# Revit family: Legrand Flush-mounting cabinets Nedbox
name_source: partatom
category: Installations électriques
units: mm (PartAtom-declared; Revit-internal decimal feet)

## family parameters
Basée sur le plan de construction = Non
Conserver l'orientation des annotations = Non
Cote de connecteur circulaire = Utiliser le diamètre
Couper avec des vides une fois chargée = Non
Numéro OmniClass = 23.80.00.00
Partagée = Non
Point de calcul de pièce = Non
Titre OmniClass = Electric Power and Lighting
Toujours verticalement = Oui
Type d'élément = Normal

## types (40) — shared parameters
Assembly Plastic door 1R 8M = Non
Assembly Plastic door transparent 1R 8M = Non
Fabricant = Legrand
Maximum permissible current = 63 A
Modèle = Nedbox
Number of modules per row = 12+2
Recessed depth = 90 mm  [stored 0.295276 ft]
Recessed width = 330 mm
URL = www.legrand.com
width = 350 mm  [stored 1.14829 ft]
zero-valued in all types: Elévation par défaut

## per-type parameters (varying)
- Flush-mounting cabinet Nedbox 12 modules Plastic door 001411: Assembly Plastic door 1R=Oui; Assembly Plastic door 2R=Non; Assembly Plastic door 3R=Non; Assembly Plastic door 4R=Non; Assembly Plastic door transparent 1R=Non; Assembly Plastic door transparent 2R=Non; Assembly Plastic door transparent 3R=Non; Assembly Plastic door transparent 4R=Non; Assembly glass metal door 1R=Non; Assembly glass metal door 2R=Non; Assembly glass metal door 3R=Non; Assembly glass metal door 4R=Non; Assembly metal door 1R=Non; Assembly metal door 2R=Non; Assembly metal door 3R=Non; Assembly metal door 4R=Non; Cabinet 001411=Oui; Cabinet 001412=Non; Cabinet 001413=Non; Cabinet 001414=Non; Cabinet 001421=Non; Cabinet 001422=Non; Cabinet 001423=Non; Cabinet 001424=Non; Cabinet 001431=Non; Cabinet 001432=Non; Cabinet 001433=Non; Cabinet 001434=Non; Cabinet 001436=Non; Cabinet 001437=Non; Cabinet 001438=Non; Cabinet 001439=Non; Cabinet 001441=Non; Cabinet 001442=Non; Cabinet 001443=Non; Cabinet 001444=Non; Cabinet 001451=Non; Cabinet 001452=Non; Cabinet 001453=Non; Cabinet 001454=Non; Cabinet 201411=Non; Cabinet 201412=Non; Cabinet 201413=Non; Cabinet 201414=Non; Cabinet 201421=Non; Cabinet 201422=Non; Cabinet 201423=Non; Cabinet 201424=Non; Cabinet 201431=Non; Cabinet 201432=Non; Cabinet 201433=Non; Cabinet 201434=Non; Cabinet HL12F=Non; Cabinet HL24F=Non; Cabinet HL36F=Non; Cabinet HL48F=Non; Number of rows=1; Plastic door=Oui; Recessed height=305 mm  [stored 1.00066 ft]; Terminal block E=13 connections Icc 10kA; glass metal door=Non; height=335 mm  [stored 1.09908 ft]; metal door=Non; transparent door=Non
- Flush-mounting cabinet Nedbox 24 modules Plastic door 001412: Assembly Plastic door 1R=Non; Assembly Plastic door 2R=Oui; Assembly Plastic door 3R=Non; Assembly Plastic door 4R=Non; Assembly Plastic door transparent 1R=Non; Assembly Plastic door transparent 2R=Non; Assembly Plastic door transparent 3R=Non; Assembly Plastic door transparent 4R=Non; Assembly glass metal door 1R=Non; Assembly glass metal door 2R=Non; Assembly glass metal door 3R=Non; Assembly glass metal door 4R=Non; Assembly metal door 1R=Non; Assembly metal door 2R=Non; Assembly metal door 3R=Non; Assembly metal door 4R=Non; Cabinet 001411=Non; Cabinet 001412=Oui; Cabinet 001413=Non; Cabinet 001414=Non; Cabinet 001421=Non; Cabinet 001422=Non; Cabinet 001423=Non; Cabinet 001424=Non; Cabinet 001431=Non; Cabinet 001432=Non; Cabinet 001433=Non; Cabinet 001434=Non; Cabinet 001436=Non; Cabinet 001437=Non; Cabinet 001438=Non; Cabinet 001439=Non; Cabinet 001441=Non; Cabinet 001442=Non; Cabinet 001443=Non; Cabinet 001444=Non; Cabinet 001451=Non; Cabinet 001452=Non; Cabinet 001453=Non; Cabinet 001454=Non; Cabinet 201411=Non; Cabinet 201412=Non; Cabinet 201413=Non; Cabinet 201414=Non; Cabinet 201421=Non; Cabinet 201422=Non; Cabinet 201423=Non; Cabinet 201424=Non; Cabinet 201431=Non; Cabinet 201432=Non; Cabinet 201433=Non; Cabinet 201434=Non; Cabinet HL12F=Non; Cabinet HL24F=Non; Cabinet HL36F=Non; Cabinet HL48F=Non; General Conditions of Use=https://export.legrand.com; Number of rows=2; Plastic door=Oui; Recessed height=430 mm; Terminal block E=17 connections Icc 10kA; glass metal door=Non; height=460 mm  [stored 1.50919 ft]; metal door=Non; transparent door=Non
- Flush-mounting cabinet Nedbox 36 modules Plastic door 001413: Assembly Plastic door 1R=Non; Assembly Plastic door 2R=Non; Assembly Plastic door 3R=Oui; Assembly Plastic door 4R=Non; Assembly Plastic door transparent 1R=Non; Assembly Plastic door transparent 2R=Non; Assembly Plastic door transparent 3R=Non; Assembly Plastic door transparent 4R=Non; Assembly glass metal door 1R=Non; Assembly glass metal door 2R=Non; Assembly glass metal door 3R=Non; Assembly glass metal door 4R=Non; Assembly metal door 1R=Non; Assembly metal door 2R=Non; Assembly metal door 3R=Non; Assembly metal door 4R=Non; Cabinet 001411=Non; Cabinet 001412=Non; Cabinet 001413=Oui; Cabinet 001414=Non; Cabinet 001421=Non; Cabinet 001422=Non; Cabinet 001423=Non; Cabinet 001424=Non; Cabinet 001431=Non; Cabinet 001432=Non; Cabinet 001433=Non; Cabinet 001434=Non; Cabinet 001436=Non; Cabinet 001437=Non; Cabinet 001438=Non; Cabinet 001439=Non; Cabinet 001441=Non; Cabinet 001442=Non; Cabinet 001443=Non; Cabinet 001444=Non; Cabinet 001451=Non; Cabinet 001452=Non; Cabinet 001453=Non; Cabinet 001454=Non; Cabinet 201411=Non; Cabinet 201412=Non; Cabinet 201413=Non; Cabinet 201414=Non; Cabinet 201421=Non; Cabinet 201422=Non; Cabinet 201423=Non; Cabinet 201424=Non; Cabinet 201431=Non; Cabinet 201432=Non; Cabinet 201433=Non; Cabinet 201434=Non; Cabinet HL12F=Non; Cabinet HL24F=Non; Cabinet HL36F=Non; Cabinet HL48F=Non; General Conditions of Use=https://export.legrand.com; Number of rows=3; Plastic door=Oui; Recessed height=555 mm  [stored 1.82087 ft]; Terminal block E=22 connections Icc 10kA; glass metal door=Non; height=585 mm  [stored 1.91929 ft]; metal door=Non; transparent door=Non
- Flush-mounting cabinet Nedbox 48 modules Plastic door 001414: Assembly Plastic door 1R=Non; Assembly Plastic door 2R=Non; Assembly Plastic door 3R=Non; Assembly Plastic door 4R=Oui; Assembly Plastic door transparent 1R=Non; Assembly Plastic door transparent 2R=Non; Assembly Plastic door transparent 3R=Non; Assembly Plastic door transparent 4R=Non; Assembly glass metal door 1R=Non; Assembly glass metal door 2R=Non; Assembly glass metal door 3R=Non; Assembly glass metal door 4R=Non; Assembly metal door 1R=Non; Assembly metal door 2R=Non; Assembly metal door 3R=Non; Assembly metal door 4R=Non; Cabinet 001411=Non; Cabinet 001412=Non; Cabinet 001413=Non; Cabinet 001414=Oui; Cabinet 001421=Non; Cabinet 001422=Non; Cabinet 001423=Non; Cabinet 001424=Non; Cabinet 001431=Non; Cabinet 001432=Non; Cabinet 001433=Non; Cabinet 001434=Non; Cabinet 001436=Non; Cabinet 001437=Non; Cabinet 001438=Non; Cabinet 001439=Non; Cabinet 001441=Non; Cabinet 001442=Non; Cabinet 001443=Non; Cabinet 001444=Non; Cabinet 001451=Non; Cabinet 001452=Non; Cabinet 001453=Non; Cabinet 001454=Non; Cabinet 201411=Non; Cabinet 201412=Non; Cabinet 201413=Non; Cabinet 201414=Non; Cabinet 201421=Non; Cabinet 201422=Non; Cabinet 201423=Non; Cabinet 201424=Non; Cabinet 201431=Non; Cabinet 201432=Non; Cabinet 201433=Non; Cabinet 201434=Non; Cabinet HL12F=Non; Cabinet HL24F=Non; Cabinet HL36F=Non; Cabinet HL48F=Non; General Conditions of Use=https://export.legrand.com; Number of rows=4; Plastic door=Oui; Recessed height=680 mm  [stored 2.23097 ft]; Terminal block E=27 connections Icc 10kA; glass metal door=Non; height=710 mm  [stored 2.3294 ft]; metal door=Non; transparent door=Non
- Flush-mounting cabinet Nedbox 12 modules transparent door 001421: Assembly Plastic door 1R=Non; Assembly Plastic door 2R=Non; Assembly Plastic door 3R=Non; Assembly Plastic door 4R=Non; Assembly Plastic door transparent 1R=Oui; Assembly Plastic door transparent 2R=Non; Assembly Plastic door transparent 3R=Non; Assembly Plastic door transparent 4R=Non; Assembly glass metal door 1R=Non; Assembly glass metal door 2R=Non; Assembly glass metal door 3R=Non; Assembly glass metal door 4R=Non; Assembly metal door 1R=Non; Assembly metal door 2R=Non; Assembly metal door 3R=Non; Assembly metal door 4R=Non; Cabinet 001411=Non; Cabinet 001412=Non; Cabinet 001413=Non; Cabinet 001414=Non; Cabinet 001421=Oui; Cabinet 001422=Non; Cabinet 001423=Non; Cabinet 001424=Non; Cabinet 001431=Non; Cabinet 001432=Non; Cabinet 001433=Non; Cabinet 001434=Non; Cabinet 001436=Non; Cabinet 001437=Non; Cabinet 001438=Non; Cabinet 001439=Non; Cabinet 001441=Non; Cabinet 001442=Non; Cabinet 001443=Non; Cabinet 001444=Non; Cabinet 001451=Non; Cabinet 001452=Non; Cabinet 001453=Non; Cabinet 001454=Non; Cabinet 201411=Non; Cabinet 201412=Non; Cabinet 201413=Non; Cabinet 201414=Non; Cabinet 201421=Non; Cabinet 201422=Non; Cabinet 201423=Non; Cabinet 201424=Non; Cabinet 201431=Non; Cabinet 201432=Non; Cabinet 201433=Non; Cabinet 201434=Non; Cabinet HL12F=Non; Cabinet HL24F=Non; Cabinet HL36F=Non; Cabinet HL48F=Non; Number of rows=1; Plastic door=Non; Recessed height=305 mm  [stored 1.00066 ft]; Terminal block E=8 connections Icc 10kA; glass metal door=Non; height=335 mm  [stored 1.09908 ft]; metal door=Non; transparent door=Oui
- Flush-mounting cabinet Nedbox 24 modules transparent door 001422: Assembly Plastic door 1R=Non; Assembly Plastic door 2R=Non; Assembly Plastic door 3R=Non; Assembly Plastic door 4R=Non; Assembly Plastic door transparent 1R=Non; Assembly Plastic door transparent 2R=Oui; Assembly Plastic door transparent 3R=Non; Assembly Plastic door transparent 4R=Non; Assembly glass metal door 1R=Non; Assembly glass metal door 2R=Non; Assembly glass metal door 3R=Non; Assembly glass metal door 4R=Non; Assembly metal door 1R=Non; Assembly metal door 2R=Non; Assembly metal door 3R=Non; Assembly metal door 4R=Non; Cabinet 001411=Non; Cabinet 001412=Non; Cabinet 001413=Non; Cabinet 001414=Non; Cabinet 001421=Non; Cabinet 001422=Oui; Cabinet 001423=Non; Cabinet 001424=Non; Cabinet 001431=Non; Cabinet 001432=Non; Cabinet 001433=Non; Cabinet 001434=Non; Cabinet 001436=Non; Cabinet 001437=Non; Cabinet 001438=Non; Cabinet 001439=Non; Cabinet 001441=Non; Cabinet 001442=Non; Cabinet 001443=Non; Cabinet 001444=Non; Cabinet 001451=Non; Cabinet 001452=Non; Cabinet 001453=Non; Cabinet 001454=Non; Cabinet 201411=Non; Cabinet 201412=Non; Cabinet 201413=Non; Cabinet 201414=Non; Cabinet 201421=Non; Cabinet 201422=Non; Cabinet 201423=Non; Cabinet 201424=Non; Cabinet 201431=Non; Cabinet 201432=Non; Cabinet 201433=Non; Cabinet 201434=Non; Cabinet HL12F=Non; Cabinet HL24F=Non; Cabinet HL36F=Non; Cabinet HL48F=Non; General Conditions of Use=https://export.legrand.com; Number of rows=2; Plastic door=Non; Recessed height=430 mm; Terminal block E=17 connections Icc 10kA; glass metal door=Non; height=460 mm  [stored 1.50919 ft]; metal door=Non; transparent door=Oui
- Flush-mounting cabinet Nedbox 36 modules transparent door 001423: Assembly Plastic door 1R=Non; Assembly Plastic door 2R=Non; Assembly Plastic door 3R=Non; Assembly Plastic door 4R=Non; Assembly Plastic door transparent 1R=Non; Assembly Plastic door transparent 2R=Non; Assembly Plastic door transparent 3R=Oui; Assembly Plastic door transparent 4R=Non; Assembly glass metal door 1R=Non; Assembly glass metal door 2R=Non; Assembly glass metal door 3R=Non; Assembly glass metal door 4R=Non; Assembly metal door 1R=Non; Assembly metal door 2R=Non; Assembly metal door 3R=Non; Assembly metal door 4R=Non; Cabinet 001411=Non; Cabinet 001412=Non; Cabinet 001413=Non; Cabinet 001414=Non; Cabinet 001421=Non; Cabinet 001422=Non; Cabinet 001423=Oui; Cabinet 001424=Non; Cabinet 001431=Non; Cabinet 001432=Non; Cabinet 001433=Non; Cabinet 001434=Non; Cabinet 001436=Non; Cabinet 001437=Non; Cabinet 001438=Non; Cabinet 001439=Non; Cabinet 001441=Non; Cabinet 001442=Non; Cabinet 001443=Non; Cabinet 001444=Non; Cabinet 001451=Non; Cabinet 001452=Non; Cabinet 001453=Non; Cabinet 001454=Non; Cabinet 201411=Non; Cabinet 201412=Non; Cabinet 201413=Non; Cabinet 201414=Non; Cabinet 201421=Non; Cabinet 201422=Non; Cabinet 201423=Non; Cabinet 201424=Non; Cabinet 201431=Non; Cabinet 201432=Non; Cabinet 201433=Non; Cabinet 201434=Non; Cabinet HL12F=Non; Cabinet HL24F=Non; Cabinet HL36F=Non; Cabinet HL48F=Non; General Conditions of Use=https://export.legrand.com; Number of rows=3; Plastic door=Non; Recessed height=555 mm  [stored 1.82087 ft]; Terminal block E=22 connections Icc 10kA; glass metal door=Non; height=585 mm  [stored 1.91929 ft]; metal door=Non; transparent door=Oui
- Flush-mounting cabinet Nedbox 48 modules transparent door 001424: Assembly Plastic door 1R=Non; Assembly Plastic door 2R=Non; Assembly Plastic door 3R=Non; Assembly Plastic door 4R=Non; Assembly Plastic door transparent 1R=Non; Assembly Plastic door transparent 2R=Non; Assembly Plastic door transparent 3R=Non; Assembly Plastic door transparent 4R=Oui; Assembly glass metal door 1R=Non; Assembly glass metal door 2R=Non; Assembly glass metal door 3R=Non; Assembly glass metal door 4R=Non; Assembly metal door 1R=Non; Assembly metal door 2R=Non; Assembly metal door 3R=Non; Assembly metal door 4R=Non; Cabinet 001411=Non; Cabinet 001412=Non; Cabinet 001413=Non; Cabinet 001414=Non; Cabinet 001421=Non; Cabinet 001422=Non; Cabinet 001423=Non; Cabinet 001424=Oui; Cabinet 001431=Non; Cabinet 001432=Non; Cabinet 001433=Non; Cabinet 001434=Non; Cabinet 001436=Non; Cabinet 001437=Non; Cabinet 001438=Non; Cabinet 001439=Non; Cabinet 001441=Non; Cabinet 001442=Non; Cabinet 001443=Non; Cabinet 001444=Non; Cabinet 001451=Non; Cabinet 001452=Non; Cabinet 001453=Non; Cabinet 001454=Non; Cabinet 201411=Non; Cabinet 201412=Non; Cabinet 201413=Non; Cabinet 201414=Non; Cabinet 201421=Non; Cabinet 201422=Non; Cabinet 201423=Non; Cabinet 201424=Non; Cabinet 201431=Non; Cabinet 201432=Non; Cabinet 201433=Non; Cabinet 201434=Non; Cabinet HL12F=Non; Cabinet HL24F=Non; Cabinet HL36F=Non; Cabinet HL48F=Non; General Conditions of Use=https://export.legrand.com; Number of rows=4; Plastic door=Non; Recessed height=680 mm  [stored 2.23097 ft]; Terminal block E=27 connections Icc 10kA; glass metal door=Non; height=710 mm  [stored 2.3294 ft]; metal door=Non; transparent door=Oui
- Flush-mounting cabinet Nedbox 12 modules metal door 001431: Assembly Plastic door 1R=Non; Assembly Plastic door 2R=Non; Assembly Plastic door 3R=Non; Assembly Plastic door 4R=Non; Assembly Plastic door transparent 1R=Non; Assembly Plastic door transparent 2R=Non; Assembly Plastic door transparent 3R=Non; Assembly Plastic door transparent 4R=Non; Assembly glass metal door 1R=Non; Assembly glass metal door 2R=Non; Assembly glass metal door 3R=Non; Assembly glass metal door 4R=Non; Assembly metal door 1R=Oui; Assembly metal door 2R=Non; Assembly metal door 3R=Non; Assembly metal door 4R=Non; Cabinet 001411=Non; Cabinet 001412=Non; Cabinet 001413=Non; Cabinet 001414=Non; Cabinet 001421=Non; Cabinet 001422=Non; Cabinet 001423=Non; Cabinet 001424=Non; Cabinet 001431=Oui; Cabinet 001432=Non; Cabinet 001433=Non; Cabinet 001434=Non; Cabinet 001436=Non; Cabinet 001437=Non; Cabinet 001438=Non; Cabinet 001439=Non; Cabinet 001441=Non; Cabinet 001442=Non; Cabinet 001443=Non; Cabinet 001444=Non; Cabinet 001451=Non; Cabinet 001452=Non; Cabinet 001453=Non; Cabinet 001454=Non; Cabinet 201411=Non; Cabinet 201412=Non; Cabinet 201413=Non; Cabinet 201414=Non; Cabinet 201421=Non; Cabinet 201422=Non; Cabinet 201423=Non; Cabinet 201424=Non; Cabinet 201431=Non; Cabinet 201432=Non; Cabinet 201433=Non; Cabinet 201434=Non; Cabinet HL12F=Non; Cabinet HL24F=Non; Cabinet HL36F=Non; Cabinet HL48F=Non; Number of rows=1; Plastic door=Non; Recessed height=305 mm  [stored 1.00066 ft]; Terminal block E=13 connections Icc 10kA; glass metal door=Non; height=335 mm  [stored 1.09908 ft]; metal door=Oui; transparent door=Non
- Flush-mounting cabinet Nedbox 24 modules metal door 001432: Assembly Plastic door 1R=Non; Assembly Plastic door 2R=Non; Assembly Plastic door 3R=Non; Assembly Plastic door 4R=Non; Assembly Plastic door transparent 1R=Non; Assembly Plastic door transparent 2R=Non; Assembly Plastic door transparent 3R=Non; Assembly Plastic door transparent 4R=Non; Assembly glass metal door 1R=Non; Assembly glass metal door 2R=Non; Assembly glass metal door 3R=Non; Assembly glass metal door 4R=Non; Assembly metal door 1R=Non; Assembly metal door 2R=Oui; Assembly metal door 3R=Non; Assembly metal door 4R=Non; Cabinet 001411=Non; Cabinet 001412=Non; Cabinet 001413=Non; Cabinet 001414=Non; Cabinet 001421=Non; Cabinet 001422=Non; Cabinet 001423=Non; Cabinet 001424=Non; Cabinet 001431=Non; Cabinet 001432=Oui; Cabinet 001433=Non; Cabinet 001434=Non; Cabinet 001436=Non; Cabinet 001437=Non; Cabinet 001438=Non; Cabinet 001439=Non; Cabinet 001441=Non; Cabinet 001442=Non; Cabinet 001443=Non; Cabinet 001444=Non; Cabinet 001451=Non; Cabinet 001452=Non; Cabinet 001453=Non; Cabinet 001454=Non; Cabinet 201411=Non; Cabinet 201412=Non; Cabinet 201413=Non; Cabinet 201414=Non; Cabinet 201421=Non; Cabinet 201422=Non; Cabinet 201423=Non; Cabinet 201424=Non; Cabinet 201431=Non; Cabinet 201432=Non; Cabinet 201433=Non; Cabinet 201434=Non; Cabinet HL12F=Non; Cabinet HL24F=Non; Cabinet HL36F=Non; Cabinet HL48F=Non; General Conditions of Use=https://export.legrand.com; Number of rows=2; Plastic door=Non; Recessed height=430 mm; Terminal block E=17 connections Icc 10kA; glass metal door=Non; height=460 mm  [stored 1.50919 ft]; metal door=Oui; transparent door=Non
- Flush-mounting cabinet Nedbox 36 modules metal door 001433: Assembly Plastic door 1R=Non; Assembly Plastic door 2R=Non; Assembly Plastic door 3R=Non; Assembly Plastic door 4R=Non; Assembly Plastic door transparent 1R=Non; Assembly Plastic door transparent 2R=Non; Assembly Plastic door transparent 3R=Non; Assembly Plastic door transparent 4R=Non; Assembly glass metal door 1R=Non; Assembly glass metal door 2R=Non; Assembly glass metal door 3R=Non; Assembly glass metal door 4R=Non; Assembly metal door 1R=Non; Assembly metal door 2R=Non; Assembly metal door 3R=Oui; Assembly metal door 4R=Non; Cabinet 001411=Non; Cabinet 001412=Non; Cabinet 001413=Non; Cabinet 001414=Non; Cabinet 001421=Non; Cabinet 001422=Non; Cabinet 001423=Non; Cabinet 001424=Non; Cabinet 001431=Non; Cabinet 001432=Non; Cabinet 001433=Oui; Cabinet 001434=Non; Cabinet 001436=Non; Cabinet 001437=Non; Cabinet 001438=Non; Cabinet 001439=Non; Cabinet 001441=Non; Cabinet 001442=Non; Cabinet 001443=Non; Cabinet 001444=Non; Cabinet 001451=Non; Cabinet 001452=Non; Cabinet 001453=Non; Cabinet 001454=Non; Cabinet 201411=Non; Cabinet 201412=Non; Cabinet 201413=Non; Cabinet 201414=Non; Cabinet 201421=Non; Cabinet 201422=Non; Cabinet 201423=Non; Cabinet 201424=Non; Cabinet 201431=Non; Cabinet 201432=Non; Cabinet 201433=Non; Cabinet 201434=Non; Cabinet HL12F=Non; Cabinet HL24F=Non; Cabinet HL36F=Non; Cabinet HL48F=Non; General Conditions of Use=https://export.legrand.com; Number of rows=3; Plastic door=Non; Recessed height=555 mm  [stored 1.82087 ft]; Terminal block E=22 connections Icc 10kA; glass metal door=Non; height=585 mm  [stored 1.91929 ft]; metal door=Oui; transparent door=Non
- Flush-mounting cabinet Nedbox 48 modules metal door 001434: Assembly Plastic door 1R=Non; Assembly Plastic door 2R=Non; Assembly Plastic door 3R=Non; Assembly Plastic door 4R=Non; Assembly Plastic door transparent 1R=Non; Assembly Plastic door transparent 2R=Non; Assembly Plastic door transparent 3R=Non; Assembly Plastic door transparent 4R=Non; Assembly glass metal door 1R=Non; Assembly glass metal door 2R=Non; Assembly glass metal door 3R=Non; Assembly glass metal door 4R=Non; Assembly metal door 1R=Non; Assembly metal door 2R=Non; Assembly metal door 3R=Non; Assembly metal door 4R=Oui; Cabinet 001411=Non; Cabinet 001412=Non; Cabinet 001413=Non; Cabinet 001414=Non; Cabinet 001421=Non; Cabinet 001422=Non; Cabinet 001423=Non; Cabinet 001424=Non; Cabinet 001431=Non; Cabinet 001432=Non; Cabinet 001433=Non; Cabinet 001434=Oui; Cabinet 001436=Non; Cabinet 001437=Non; Cabinet 001438=Non; Cabinet 001439=Non; Cabinet 001441=Non; Cabinet 001442=Non; Cabinet 001443=Non; Cabinet 001444=Non; Cabinet 001451=Non; Cabinet 001452=Non; Cabinet 001453=Non; Cabinet 001454=Non; Cabinet 201411=Non; Cabinet 201412=Non; Cabinet 201413=Non; Cabinet 201414=Non; Cabinet 201421=Non; Cabinet 201422=Non; Cabinet 201423=Non; Cabinet 201424=Non; Cabinet 201431=Non; Cabinet 201432=Non; Cabinet 201433=Non; Cabinet 201434=Non; Cabinet HL12F=Non; Cabinet HL24F=Non; Cabinet HL36F=Non; Cabinet HL48F=Non; General Conditions of Use=https://export.legrand.com; Number of rows=4; Plastic door=Non; Recessed height=680 mm  [stored 2.23097 ft]; Terminal block E=27 connections Icc 10kA; glass metal door=Non; height=710 mm  [stored 2.3294 ft]; metal door=Oui; transparent door=Non
- Flush-mounting cabinet Nedbox 12 modules metal door 001436: Assembly Plastic door 1R=Non; Assembly Plastic door 2R=Non; Assembly Plastic door 3R=Non; Assembly Plastic door 4R=Non; Assembly Plastic door transparent 1R=Non; Assembly Plastic door transparent 2R=Non; Assembly Plastic door transparent 3R=Non; Assembly Plastic door transparent 4R=Non; Assembly glass metal door 1R=Non; Assembly glass metal door 2R=Non; Assembly glass metal door 3R=Non; Assembly glass metal door 4R=Non; Assembly metal door 1R=Oui; Assembly metal door 2R=Non; Assembly metal door 3R=Non; Assembly metal door 4R=Non; Cabinet 001411=Non; Cabinet 001412=Non; Cabinet 001413=Non; Cabinet 001414=Non; Cabinet 001421=Non; Cabinet 001422=Non; Cabinet 001423=Non; Cabinet 001424=Non; Cabinet 001431=Non; Cabinet 001432=Non; Cabinet 001433=Non; Cabinet 001434=Non; Cabinet 001436=Oui; Cabinet 001437=Non; Cabinet 001438=Non; Cabinet 001439=Non; Cabinet 001441=Non; Cabinet 001442=Non; Cabinet 001443=Non; Cabinet 001444=Non; Cabinet 001451=Non; Cabinet 001452=Non; Cabinet 001453=Non; Cabinet 001454=Non; Cabinet 201411=Non; Cabinet 201412=Non; Cabinet 201413=Non; Cabinet 201414=Non; Cabinet 201421=Non; Cabinet 201422=Non; Cabinet 201423=Non; Cabinet 201424=Non; Cabinet 201431=Non; Cabinet 201432=Non; Cabinet 201433=Non; Cabinet 201434=Non; Cabinet HL12F=Non; Cabinet HL24F=Non; Cabinet HL36F=Non; Cabinet HL48F=Non; Number of rows=1; Plastic door=Non; Recessed height=305 mm  [stored 1.00066 ft]; Terminal block E=12 connections Icc 6kA; Terminal block N=12 connections Icc 6kA; glass metal door=Non; height=335 mm  [stored 1.09908 ft]; metal door=Oui; transparent door=Non
- Flush-mounting cabinet Nedbox 24 modules metal door 001437: Assembly Plastic door 1R=Non; Assembly Plastic door 2R=Non; Assembly Plastic door 3R=Non; Assembly Plastic door 4R=Non; Assembly Plastic door transparent 1R=Non; Assembly Plastic door transparent 2R=Non; Assembly Plastic door transparent 3R=Non; Assembly Plastic door transparent 4R=Non; Assembly glass metal door 1R=Non; Assembly glass metal door 2R=Non; Assembly glass metal door 3R=Non; Assembly glass metal door 4R=Non; Assembly metal door 1R=Non; Assembly metal door 2R=Oui; Assembly metal door 3R=Non; Assembly metal door 4R=Non; Cabinet 001411=Non; Cabinet 001412=Non; Cabinet 001413=Non; Cabinet 001414=Non; Cabinet 001421=Non; Cabinet 001422=Non; Cabinet 001423=Non; Cabinet 001424=Non; Cabinet 001431=Non; Cabinet 001432=Non; Cabinet 001433=Non; Cabinet 001434=Non; Cabinet 001436=Non; Cabinet 001437=Oui; Cabinet 001438=Non; Cabinet 001439=Non; Cabinet 001441=Non; Cabinet 001442=Non; Cabinet 001443=Non; Cabinet 001444=Non; Cabinet 001451=Non; Cabinet 001452=Non; Cabinet 001453=Non; Cabinet 001454=Non; Cabinet 201411=Non; Cabinet 201412=Non; Cabinet 201413=Non; Cabinet 201414=Non; Cabinet 201421=Non; Cabinet 201422=Non; Cabinet 201423=Non; Cabinet 201424=Non; Cabinet 201431=Non; Cabinet 201432=Non; Cabinet 201433=Non; Cabinet 201434=Non; Cabinet HL12F=Non; Cabinet HL24F=Non; Cabinet HL36F=Non; Cabinet HL48F=Non; General Conditions of Use=https://export.legrand.com; Number of rows=2; Plastic door=Non; Recessed height=430 mm; Terminal block E=16 connections Icc 6kA; Terminal block N=2X 8 connections Icc 6kA; glass metal door=Non; height=460 mm  [stored 1.50919 ft]; metal door=Oui; transparent door=Non
- Flush-mounting cabinet Nedbox 36 modules metal door 001438: Assembly Plastic door 1R=Non; Assembly Plastic door 2R=Non; Assembly Plastic door 3R=Non; Assembly Plastic door 4R=Non; Assembly Plastic door transparent 1R=Non; Assembly Plastic door transparent 2R=Non; Assembly Plastic door transparent 3R=Non; Assembly Plastic door transparent 4R=Non; Assembly glass metal door 1R=Non; Assembly glass metal door 2R=Non; Assembly glass metal door 3R=Non; Assembly glass metal door 4R=Non; Assembly metal door 1R=Non; Assembly metal door 2R=Non; Assembly metal door 3R=Oui; Assembly metal door 4R=Non; Cabinet 001411=Non; Cabinet 001412=Non; Cabinet 001413=Non; Cabinet 001414=Non; Cabinet 001421=Non; Cabinet 001422=Non; Cabinet 001423=Non; Cabinet 001424=Non; Cabinet 001431=Non; Cabinet 001432=Non; Cabinet 001433=Non; Cabinet 001434=Non; Cabinet 001436=Non; Cabinet 001437=Non; Cabinet 001438=Oui; Cabinet 001439=Non; Cabinet 001441=Non; Cabinet 001442=Non; Cabinet 001443=Non; Cabinet 001444=Non; Cabinet 001451=Non; Cabinet 001452=Non; Cabinet 001453=Non; Cabinet 001454=Non; Cabinet 201411=Non; Cabinet 201412=Non; Cabinet 201413=Non; Cabinet 201414=Non; Cabinet 201421=Non; Cabinet 201422=Non; Cabinet 201423=Non; Cabinet 201424=Non; Cabinet 201431=Non; Cabinet 201432=Non; Cabinet 201433=Non; Cabinet 201434=Non; Cabinet HL12F=Non; Cabinet HL24F=Non; Cabinet HL36F=Non; Cabinet HL48F=Non; General Conditions of Use=https://export.legrand.com; Number of rows=3; Plastic door=Non; Recessed height=555 mm  [stored 1.82087 ft]; Terminal block E=30 connections Icc 6kA; Terminal block N=2X 12 connections Icc 6kA; glass metal door=Non; height=585 mm  [stored 1.91929 ft]; metal door=Oui; transparent door=Non
- Flush-mounting cabinet Nedbox 48 modules metal door 001439: Assembly Plastic door 1R=Non; Assembly Plastic door 2R=Non; Assembly Plastic door 3R=Non; Assembly Plastic door 4R=Non; Assembly Plastic door transparent 1R=Non; Assembly Plastic door transparent 2R=Non; Assembly Plastic door transparent 3R=Non; Assembly Plastic door transparent 4R=Non; Assembly glass metal door 1R=Non; Assembly glass metal door 2R=Non; Assembly glass metal door 3R=Non; Assembly glass metal door 4R=Non; Assembly metal door 1R=Non; Assembly metal door 2R=Non; Assembly metal door 3R=Non; Assembly metal door 4R=Oui; Cabinet 001411=Non; Cabinet 001412=Non; Cabinet 001413=Non; Cabinet 001414=Non; Cabinet 001421=Non; Cabinet 001422=Non; Cabinet 001423=Non; Cabinet 001424=Non; Cabinet 001431=Non; Cabinet 001432=Non; Cabinet 001433=Non; Cabinet 001434=Non; Cabinet 001436=Non; Cabinet 001437=Non; Cabinet 001438=Non; Cabinet 001439=Oui; Cabinet 001441=Non; Cabinet 001442=Non; Cabinet 001443=Non; Cabinet 001444=Non; Cabinet 001451=Non; Cabinet 001452=Non; Cabinet 001453=Non; Cabinet 001454=Non; Cabinet 201411=Non; Cabinet 201412=Non; Cabinet 201413=Non; Cabinet 201414=Non; Cabinet 201421=Non; Cabinet 201422=Non; Cabinet 201423=Non; Cabinet 201424=Non; Cabinet 201431=Non; Cabinet 201432=Non; Cabinet 201433=Non; Cabinet 201434=Non; Cabinet HL12F=Non; Cabinet HL24F=Non; Cabinet HL36F=Non; Cabinet HL48F=Non; General Conditions of Use=https://export.legrand.com; Number of rows=4; Plastic door=Non; Recessed height=680 mm  [stored 2.23097 ft]; Terminal block E=30 connections Icc 6kA; Terminal block N=2X 12 connections Icc 6kA; glass metal door=Non; height=710 mm  [stored 2.3294 ft]; metal door=Oui; transparent door=Non
- Flush-mounting cabinet Nedbox 12 modules metal door 001441: Assembly Plastic door 1R=Non; Assembly Plastic door 2R=Non; Assembly Plastic door 3R=Non; Assembly Plastic door 4R=Non; Assembly Plastic door transparent 1R=Non; Assembly Plastic door transparent 2R=Non; Assembly Plastic door transparent 3R=Non; Assembly Plastic door transparent 4R=Non; Assembly glass metal door 1R=Non; Assembly glass metal door 2R=Non; Assembly glass metal door 3R=Non; Assembly glass metal door 4R=Non; Assembly metal door 1R=Oui; Assembly metal door 2R=Non; Assembly metal door 3R=Non; Assembly metal door 4R=Non; Cabinet 001411=Non; Cabinet 001412=Non; Cabinet 001413=Non; Cabinet 001414=Non; Cabinet 001421=Non; Cabinet 001422=Non; Cabinet 001423=Non; Cabinet 001424=Non; Cabinet 001431=Non; Cabinet 001432=Non; Cabinet 001433=Non; Cabinet 001434=Non; Cabinet 001436=Non; Cabinet 001437=Non; Cabinet 001438=Non; Cabinet 001439=Non; Cabinet 001441=Oui; Cabinet 001442=Non; Cabinet 001443=Non; Cabinet 001444=Non; Cabinet 001451=Non; Cabinet 001452=Non; Cabinet 001453=Non; Cabinet 001454=Non; Cabinet 201411=Non; Cabinet 201412=Non; Cabinet 201413=Non; Cabinet 201414=Non; Cabinet 201421=Non; Cabinet 201422=Non; Cabinet 201423=Non; Cabinet 201424=Non; Cabinet 201431=Non; Cabinet 201432=Non; Cabinet 201433=Non; Cabinet 201434=Non; Cabinet HL12F=Non; Cabinet HL24F=Non; Cabinet HL36F=Non; Cabinet HL48F=Non; Number of rows=1; Plastic door=Non; Recessed height=305 mm  [stored 1.00066 ft]; Terminal block E=12 connections Icc 6kA; Terminal block N=12 connections Icc 6kA; glass metal door=Non; height=335 mm  [stored 1.09908 ft]; metal door=Oui; transparent door=Non
- Flush-mounting cabinet Nedbox 24 modules metal door 001442: Assembly Plastic door 1R=Non; Assembly Plastic door 2R=Non; Assembly Plastic door 3R=Non; Assembly Plastic door 4R=Non; Assembly Plastic door transparent 1R=Non; Assembly Plastic door transparent 2R=Non; Assembly Plastic door transparent 3R=Non; Assembly Plastic door transparent 4R=Non; Assembly glass metal door 1R=Non; Assembly glass metal door 2R=Non; Assembly glass metal door 3R=Non; Assembly glass metal door 4R=Non; Assembly metal door 1R=Non; Assembly metal door 2R=Oui; Assembly metal door 3R=Non; Assembly metal door 4R=Non; Cabinet 001411=Non; Cabinet 001412=Non; Cabinet 001413=Non; Cabinet 001414=Non; Cabinet 001421=Non; Cabinet 001422=Non; Cabinet 001423=Non; Cabinet 001424=Non; Cabinet 001431=Non; Cabinet 001432=Non; Cabinet 001433=Non; Cabinet 001434=Non; Cabinet 001436=Non; Cabinet 001437=Non; Cabinet 001438=Non; Cabinet 001439=Non; Cabinet 001441=Non; Cabinet 001442=Oui; Cabinet 001443=Non; Cabinet 001444=Non; Cabinet 001451=Non; Cabinet 001452=Non; Cabinet 001453=Non; Cabinet 001454=Non; Cabinet 201411=Non; Cabinet 201412=Non; Cabinet 201413=Non; Cabinet 201414=Non; Cabinet 201421=Non; Cabinet 201422=Non; Cabinet 201423=Non; Cabinet 201424=Non; Cabinet 201431=Non; Cabinet 201432=Non; Cabinet 201433=Non; Cabinet 201434=Non; Cabinet HL12F=Non; Cabinet HL24F=Non; Cabinet HL36F=Non; Cabinet HL48F=Non; General Conditions of Use=https://export.legrand.com; Number of rows=2; Plastic door=Non; Recessed height=430 mm; Terminal block E=16 connections Icc 6kA; Terminal block N=2X 8 connections Icc 6kA; glass metal door=Non; height=460 mm  [stored 1.50919 ft]; metal door=Oui; transparent door=Non
- Flush-mounting cabinet Nedbox 36 modules metal door 001443: Assembly Plastic door 1R=Non; Assembly Plastic door 2R=Non; Assembly Plastic door 3R=Non; Assembly Plastic door 4R=Non; Assembly Plastic door transparent 1R=Non; Assembly Plastic door transparent 2R=Non; Assembly Plastic door transparent 3R=Non; Assembly Plastic door transparent 4R=Non; Assembly glass metal door 1R=Non; Assembly glass metal door 2R=Non; Assembly glass metal door 3R=Non; Assembly glass metal door 4R=Non; Assembly metal door 1R=Non; Assembly metal door 2R=Non; Assembly metal door 3R=Oui; Assembly metal door 4R=Non; Cabinet 001411=Non; Cabinet 001412=Non; Cabinet 001413=Non; Cabinet 001414=Non; Cabinet 001421=Non; Cabinet 001422=Non; Cabinet 001423=Non; Cabinet 001424=Non; Cabinet 001431=Non; Cabinet 001432=Non; Cabinet 001433=Non; Cabinet 001434=Non; Cabinet 001436=Non; Cabinet 001437=Non; Cabinet 001438=Non; Cabinet 001439=Non; Cabinet 001441=Non; Cabinet 001442=Non; Cabinet 001443=Oui; Cabinet 001444=Non; Cabinet 001451=Non; Cabinet 001452=Non; Cabinet 001453=Non; Cabinet 001454=Non; Cabinet 201411=Non; Cabinet 201412=Non; Cabinet 201413=Non; Cabinet 201414=Non; Cabinet 201421=Non; Cabinet 201422=Non; Cabinet 201423=Non; Cabinet 201424=Non; Cabinet 201431=Non; Cabinet 201432=Non; Cabinet 201433=Non; Cabinet 201434=Non; Cabinet HL12F=Non; Cabinet HL24F=Non; Cabinet HL36F=Non; Cabinet HL48F=Non; General Conditions of Use=https://export.legrand.com; Number of rows=3; Plastic door=Non; Recessed height=555 mm  [stored 1.82087 ft]; Terminal block E=30 connections Icc 6kA; Terminal block N=2X 12 connections Icc 6kA; glass metal door=Non; height=585 mm  [stored 1.91929 ft]; metal door=Oui; transparent door=Non
- Flush-mounting cabinet Nedbox 48 modules metal door 001444: Assembly Plastic door 1R=Non; Assembly Plastic door 2R=Non; Assembly Plastic door 3R=Non; Assembly Plastic door 4R=Non; Assembly Plastic door transparent 1R=Non; Assembly Plastic door transparent 2R=Non; Assembly Plastic door transparent 3R=Non; Assembly Plastic door transparent 4R=Non; Assembly glass metal door 1R=Non; Assembly glass metal door 2R=Non; Assembly glass metal door 3R=Non; Assembly glass metal door 4R=Non; Assembly metal door 1R=Non; Assembly metal door 2R=Non; Assembly metal door 3R=Non; Assembly metal door 4R=Oui; Cabinet 001411=Non; Cabinet 001412=Non; Cabinet 001413=Non; Cabinet 001414=Non; Cabinet 001421=Non; Cabinet 001422=Non; Cabinet 001423=Non; Cabinet 001424=Non; Cabinet 001431=Non; Cabinet 001432=Non; Cabinet 001433=Non; Cabinet 001434=Non; Cabinet 001436=Non; Cabinet 001437=Non; Cabinet 001438=Non; Cabinet 001439=Non; Cabinet 001441=Non; Cabinet 001442=Non; Cabinet 001443=Non; Cabinet 001444=Oui; Cabinet 001451=Non; Cabinet 001452=Non; Cabinet 001453=Non; Cabinet 001454=Non; Cabinet 201411=Non; Cabinet 201412=Non; Cabinet 201413=Non; Cabinet 201414=Non; Cabinet 201421=Non; Cabinet 201422=Non; Cabinet 201423=Non; Cabinet 201424=Non; Cabinet 201431=Non; Cabinet 201432=Non; Cabinet 201433=Non; Cabinet 201434=Non; Cabinet HL12F=Non; Cabinet HL24F=Non; Cabinet HL36F=Non; Cabinet HL48F=Non; General Conditions of Use=https://export.legrand.com; Number of rows=4; Plastic door=Non; Recessed height=680 mm  [stored 2.23097 ft]; Terminal block E=30 connections Icc 6kA; Terminal block N=3X 12 connections Icc 6kA; glass metal door=Non; height=710 mm  [stored 2.3294 ft]; metal door=Oui; transparent door=Non
- Flush-mounting cabinet Nedbox 12 modules glass metal door 001451: Assembly Plastic door 1R=Non; Assembly Plastic door 2R=Non; Assembly Plastic door 3R=Non; Assembly Plastic door 4R=Non; Assembly Plastic door transparent 1R=Non; Assembly Plastic door transparent 2R=Non; Assembly Plastic door transparent 3R=Non; Assembly Plastic door transparent 4R=Non; Assembly glass metal door 1R=Oui; Assembly glass metal door 2R=Non; Assembly glass metal door 3R=Non; Assembly glass metal door 4R=Non; Assembly metal door 1R=Non; Assembly metal door 2R=Non; Assembly metal door 3R=Non; Assembly metal door 4R=Non; Cabinet 001411=Non; Cabinet 001412=Non; Cabinet 001413=Non; Cabinet 001414=Non; Cabinet 001421=Non; Cabinet 001422=Non; Cabinet 001423=Non; Cabinet 001424=Non; Cabinet 001431=Non; Cabinet 001432=Non; Cabinet 001433=Non; Cabinet 001434=Non; Cabinet 001436=Non; Cabinet 001437=Non; Cabinet 001438=Non; Cabinet 001439=Non; Cabinet 001441=Non; Cabinet 001442=Non; Cabinet 001443=Non; Cabinet 001444=Non; Cabinet 001451=Oui; Cabinet 001452=Non; Cabinet 001453=Non; Cabinet 001454=Non; Cabinet 201411=Non; Cabinet 201412=Non; Cabinet 201413=Non; Cabinet 201414=Non; Cabinet 201421=Non; Cabinet 201422=Non; Cabinet 201423=Non; Cabinet 201424=Non; Cabinet 201431=Non; Cabinet 201432=Non; Cabinet 201433=Non; Cabinet 201434=Non; Cabinet HL12F=Non; Cabinet HL24F=Non; Cabinet HL36F=Non; Cabinet HL48F=Non; Number of rows=1; Plastic door=Non; Recessed height=305 mm  [stored 1.00066 ft]; Terminal block E=12 connections Icc 6kA; Terminal block N=12 connections Icc 6kA; glass metal door=Oui; height=335 mm  [stored 1.09908 ft]; metal door=Non; transparent door=Non
- Flush-mounting cabinet Nedbox 24 modules glass metal door 001452: Assembly Plastic door 1R=Non; Assembly Plastic door 2R=Non; Assembly Plastic door 3R=Non; Assembly Plastic door 4R=Non; Assembly Plastic door transparent 1R=Non; Assembly Plastic door transparent 2R=Non; Assembly Plastic door transparent 3R=Non; Assembly Plastic door transparent 4R=Non; Assembly glass metal door 1R=Non; Assembly glass metal door 2R=Oui; Assembly glass metal door 3R=Non; Assembly glass metal door 4R=Non; Assembly metal door 1R=Non; Assembly metal door 2R=Non; Assembly metal door 3R=Non; Assembly metal door 4R=Non; Cabinet 001411=Non; Cabinet 001412=Non; Cabinet 001413=Non; Cabinet 001414=Non; Cabinet 001421=Non; Cabinet 001422=Non; Cabinet 001423=Non; Cabinet 001424=Non; Cabinet 001431=Non; Cabinet 001432=Non; Cabinet 001433=Non; Cabinet 001434=Non; Cabinet 001436=Non; Cabinet 001437=Non; Cabinet 001438=Non; Cabinet 001439=Non; Cabinet 001441=Non; Cabinet 001442=Non; Cabinet 001443=Non; Cabinet 001444=Non; Cabinet 001451=Non; Cabinet 001452=Oui; Cabinet 001453=Non; Cabinet 001454=Non; Cabinet 201411=Non; Cabinet 201412=Non; Cabinet 201413=Non; Cabinet 201414=Non; Cabinet 201421=Non; Cabinet 201422=Non; Cabinet 201423=Non; Cabinet 201424=Non; Cabinet 201431=Non; Cabinet 201432=Non; Cabinet 201433=Non; Cabinet 201434=Non; Cabinet HL12F=Non; Cabinet HL24F=Non; Cabinet HL36F=Non; Cabinet HL48F=Non; General Conditions of Use=https://export.legrand.com; Number of rows=2; Plastic door=Non; Recessed height=430 mm; Terminal block E=16 connections Icc 6kA; Terminal block N=2X 8 connections Icc 6kA; glass metal door=Oui; height=460 mm  [stored 1.50919 ft]; metal door=Non; transparent door=Non
- Flush-mounting cabinet Nedbox 36 modules glass metal door 001453: Assembly Plastic door 1R=Non; Assembly Plastic door 2R=Non; Assembly Plastic door 3R=Non; Assembly Plastic door 4R=Non; Assembly Plastic door transparent 1R=Non; Assembly Plastic door transparent 2R=Non; Assembly Plastic door transparent 3R=Non; Assembly Plastic door transparent 4R=Non; Assembly glass metal door 1R=Non; Assembly glass metal door 2R=Non; Assembly glass metal door 3R=Oui; Assembly glass metal door 4R=Non; Assembly metal door 1R=Non; Assembly metal door 2R=Non; Assembly metal door 3R=Non; Assembly metal door 4R=Non; Cabinet 001411=Non; Cabinet 001412=Non; Cabinet 001413=Non; Cabinet 001414=Non; Cabinet 001421=Non; Cabinet 001422=Non; Cabinet 001423=Non; Cabinet 001424=Non; Cabinet 001431=Non; Cabinet 001432=Non; Cabinet 001433=Non; Cabinet 001434=Non; Cabinet 001436=Non; Cabinet 001437=Non; Cabinet 001438=Non; Cabinet 001439=Non; Cabinet 001441=Non; Cabinet 001442=Non; Cabinet 001443=Non; Cabinet 001444=Non; Cabinet 001451=Non; Cabinet 001452=Non; Cabinet 001453=Oui; Cabinet 001454=Non; Cabinet 201411=Non; Cabinet 201412=Non; Cabinet 201413=Non; Cabinet 201414=Non; Cabinet 201421=Non; Cabinet 201422=Non; Cabinet 201423=Non; Cabinet 201424=Non; Cabinet 201431=Non; Cabinet 201432=Non; Cabinet 201433=Non; Cabinet 201434=Non; Cabinet HL12F=Non; Cabinet HL24F=Non; Cabinet HL36F=Non; Cabinet HL48F=Non; General Conditions of Use=https://export.legrand.com; Number of rows=3; Plastic door=Non; Recessed height=555 mm  [stored 1.82087 ft]; Terminal block E=30 connections Icc 6kA; Terminal block N=2X 12 connections Icc 6kA; glass metal door=Oui; height=585 mm  [stored 1.91929 ft]; metal door=Non; transparent door=Non
- Flush-mounting cabinet Nedbox 48 modules glass metal door 001454: Assembly Plastic door 1R=Non; Assembly Plastic door 2R=Non; Assembly Plastic door 3R=Non; Assembly Plastic door 4R=Non; Assembly Plastic door transparent 1R=Non; Assembly Plastic door transparent 2R=Non; Assembly Plastic door transparent 3R=Non; Assembly Plastic door transparent 4R=Non; Assembly glass metal door 1R=Non; Assembly glass metal door 2R=Non; Assembly glass metal door 3R=Non; Assembly glass metal door 4R=Oui; Assembly metal door 1R=Non; Assembly metal door 2R=Non; Assembly metal door 3R=Non; Assembly metal door 4R=Non; Cabinet 001411=Non; Cabinet 001412=Non; Cabinet 001413=Non; Cabinet 001414=Non; Cabinet 001421=Non; Cabinet 001422=Non; Cabinet 001423=Non; Cabinet 001424=Non; Cabinet 001431=Non; Cabinet 001432=Non; Cabinet 001433=Non; Cabinet 001434=Non; Cabinet 001436=Non; Cabinet 001437=Non; Cabinet 001438=Non; Cabinet 001439=Non; Cabinet 001441=Non; Cabinet 001442=Non; Cabinet 001443=Non; Cabinet 001444=Non; Cabinet 001451=Non; Cabinet 001452=Non; Cabinet 001453=Non; Cabinet 001454=Oui; Cabinet 201411=Non; Cabinet 201412=Non; Cabinet 201413=Non; Cabinet 201414=Non; Cabinet 201421=Non; Cabinet 201422=Non; Cabinet 201423=Non; Cabinet 201424=Non; Cabinet 201431=Non; Cabinet 201432=Non; Cabinet 201433=Non; Cabinet 201434=Non; Cabinet HL12F=Non; Cabinet HL24F=Non; Cabinet HL36F=Non; Cabinet HL48F=Non; General Conditions of Use=https://export.legrand.com; Number of rows=4; Plastic door=Non; Recessed height=680 mm  [stored 2.23097 ft]; Terminal block E=30 connections Icc 6kA; Terminal block N=3X 12 connections Icc 6kA; glass metal door=Oui; height=710 mm  [stored 2.3294 ft]; metal door=Non; transparent door=Non
- Flush-mounting cabinet Nedbox 12 modules Plastic door 201411: Assembly Plastic door 1R=Oui; Assembly Plastic door 2R=Non; Assembly Plastic door 3R=Non; Assembly Plastic door 4R=Non; Assembly Plastic door transparent 1R=Non; Assembly Plastic door transparent 2R=Non; Assembly Plastic door transparent 3R=Non; Assembly Plastic door transparent 4R=Non; Assembly glass metal door 1R=Non; Assembly glass metal door 2R=Non; Assembly glass metal door 3R=Non; Assembly glass metal door 4R=Non; Assembly metal door 1R=Non; Assembly metal door 2R=Non; Assembly metal door 3R=Non; Assembly metal door 4R=Non; Cabinet 001411=Non; Cabinet 001412=Non; Cabinet 001413=Non; Cabinet 001414=Non; Cabinet 001421=Non; Cabinet 001422=Non; Cabinet 001423=Non; Cabinet 001424=Non; Cabinet 001431=Non; Cabinet 001432=Non; Cabinet 001433=Non; Cabinet 001434=Non; Cabinet 001436=Non; Cabinet 001437=Non; Cabinet 001438=Non; Cabinet 001439=Non; Cabinet 001441=Non; Cabinet 001442=Non; Cabinet 001443=Non; Cabinet 001444=Non; Cabinet 001451=Non; Cabinet 001452=Non; Cabinet 001453=Non; Cabinet 001454=Non; Cabinet 201411=Oui; Cabinet 201412=Non; Cabinet 201413=Non; Cabinet 201414=Non; Cabinet 201421=Non; Cabinet 201422=Non; Cabinet 201423=Non; Cabinet 201424=Non; Cabinet 201431=Non; Cabinet 201432=Non; Cabinet 201433=Non; Cabinet 201434=Non; Cabinet HL12F=Non; Cabinet HL24F=Non; Cabinet HL36F=Non; Cabinet HL48F=Non; Number of rows=1; Plastic door=Oui; Recessed height=305 mm  [stored 1.00066 ft]; Terminal block E=12 connections Icc 6kA; Terminal block N=12 connections Icc 6kA; glass metal door=Non; height=335 mm  [stored 1.09908 ft]; metal door=Non; transparent door=Non
- Flush-mounting cabinet Nedbox 24 modules Plastic door 201412: Assembly Plastic door 1R=Non; Assembly Plastic door 2R=Oui; Assembly Plastic door 3R=Non; Assembly Plastic door 4R=Non; Assembly Plastic door transparent 1R=Non; Assembly Plastic door transparent 2R=Non; Assembly Plastic door transparent 3R=Non; Assembly Plastic door transparent 4R=Non; Assembly glass metal door 1R=Non; Assembly glass metal door 2R=Non; Assembly glass metal door 3R=Non; Assembly glass metal door 4R=Non; Assembly metal door 1R=Non; Assembly metal door 2R=Non; Assembly metal door 3R=Non; Assembly metal door 4R=Non; Cabinet 001411=Non; Cabinet 001412=Non; Cabinet 001413=Non; Cabinet 001414=Non; Cabinet 001421=Non; Cabinet 001422=Non; Cabinet 001423=Non; Cabinet 001424=Non; Cabinet 001431=Non; Cabinet 001432=Non; Cabinet 001433=Non; Cabinet 001434=Non; Cabinet 001436=Non; Cabinet 001437=Non; Cabinet 001438=Non; Cabinet 001439=Non; Cabinet 001441=Non; Cabinet 001442=Non; Cabinet 001443=Non; Cabinet 001444=Non; Cabinet 001451=Non; Cabinet 001452=Non; Cabinet 001453=Non; Cabinet 001454=Non; Cabinet 201411=Non; Cabinet 201412=Oui; Cabinet 201413=Non; Cabinet 201414=Non; Cabinet 201421=Non; Cabinet 201422=Non; Cabinet 201423=Non; Cabinet 201424=Non; Cabinet 201431=Non; Cabinet 201432=Non; Cabinet 201433=Non; Cabinet 201434=Non; Cabinet HL12F=Non; Cabinet HL24F=Non; Cabinet HL36F=Non; Cabinet HL48F=Non; General Conditions of Use=https://export.legrand.com; Number of rows=2; Plastic door=Oui; Recessed height=430 mm; Terminal block E=16 connections Icc 6kA; Terminal block N=2X 8 connections Icc 6kA; glass metal door=Non; height=460 mm  [stored 1.50919 ft]; metal door=Non; transparent door=Non
- Flush-mounting cabinet Nedbox 36 modules Plastic door 201413: Assembly Plastic door 1R=Non; Assembly Plastic door 2R=Non; Assembly Plastic door 3R=Oui; Assembly Plastic door 4R=Non; Assembly Plastic door transparent 1R=Non; Assembly Plastic door transparent 2R=Non; Assembly Plastic door transparent 3R=Non; Assembly Plastic door transparent 4R=Non; Assembly glass metal door 1R=Non; Assembly glass metal door 2R=Non; Assembly glass metal door 3R=Non; Assembly glass metal door 4R=Non; Assembly metal door 1R=Non; Assembly metal door 2R=Non; Assembly metal door 3R=Non; Assembly metal door 4R=Non; Cabinet 001411=Non; Cabinet 001412=Non; Cabinet 001413=Non; Cabinet 001414=Non; Cabinet 001421=Non; Cabinet 001422=Non; Cabinet 001423=Non; Cabinet 001424=Non; Cabinet 001431=Non; Cabinet 001432=Non; Cabinet 001433=Non; Cabinet 001434=Non; Cabinet 001436=Non; Cabinet 001437=Non; Cabinet 001438=Non; Cabinet 001439=Non; Cabinet 001441=Non; Cabinet 001442=Non; Cabinet 001443=Non; Cabinet 001444=Non; Cabinet 001451=Non; Cabinet 001452=Non; Cabinet 001453=Non; Cabinet 001454=Non; Cabinet 201411=Non; Cabinet 201412=Non; Cabinet 201413=Oui; Cabinet 201414=Non; Cabinet 201421=Non; Cabinet 201422=Non; Cabinet 201423=Non; Cabinet 201424=Non; Cabinet 201431=Non; Cabinet 201432=Non; Cabinet 201433=Non; Cabinet 201434=Non; Cabinet HL12F=Non; Cabinet HL24F=Non; Cabinet HL36F=Non; Cabinet HL48F=Non; General Conditions of Use=https://export.legrand.com; Number of rows=3; Plastic door=Oui; Recessed height=555 mm  [stored 1.82087 ft]; Terminal block E=30 connections Icc 6kA; Terminal block N=2X 12 connections Icc 6kA; glass metal door=Non; height=585 mm  [stored 1.91929 ft]; metal door=Non; transparent door=Non
- Flush-mounting cabinet Nedbox 48 modules Plastic door 201414: Assembly Plastic door 1R=Non; Assembly Plastic door 2R=Non; Assembly Plastic door 3R=Non; Assembly Plastic door 4R=Oui; Assembly Plastic door transparent 1R=Non; Assembly Plastic door transparent 2R=Non; Assembly Plastic door transparent 3R=Non; Assembly Plastic door transparent 4R=Non; Assembly glass metal door 1R=Non; Assembly glass metal door 2R=Non; Assembly glass metal door 3R=Non; Assembly glass metal door 4R=Non; Assembly metal door 1R=Non; Assembly metal door 2R=Non; Assembly metal door 3R=Non; Assembly metal door 4R=Non; Cabinet 001411=Non; Cabinet 001412=Non; Cabinet 001413=Non; Cabinet 001414=Non; Cabinet 001421=Non; Cabinet 001422=Non; Cabinet 001423=Non; Cabinet 001424=Non; Cabinet 001431=Non; Cabinet 001432=Non; Cabinet 001433=Non; Cabinet 001434=Non; Cabinet 001436=Non; Cabinet 001437=Non; Cabinet 001438=Non; Cabinet 001439=Non; Cabinet 001441=Non; Cabinet 001442=Non; Cabinet 001443=Non; Cabinet 001444=Non; Cabinet 001451=Non; Cabinet 001452=Non; Cabinet 001453=Non; Cabinet 001454=Non; Cabinet 201411=Non; Cabinet 201412=Non; Cabinet 201413=Non; Cabinet 201414=Oui; Cabinet 201421=Non; Cabinet 201422=Non; Cabinet 201423=Non; Cabinet 201424=Non; Cabinet 201431=Non; Cabinet 201432=Non; Cabinet 201433=Non; Cabinet 201434=Non; Cabinet HL12F=Non; Cabinet HL24F=Non; Cabinet HL36F=Non; Cabinet HL48F=Non; General Conditions of Use=https://export.legrand.com; Number of rows=4; Plastic door=Oui; Recessed height=680 mm  [stored 2.23097 ft]; Terminal block E=30 connections Icc 6kA; Terminal block N=3X 12 connections Icc 6kA; glass metal door=Non; height=710 mm  [stored 2.3294 ft]; metal door=Non; transparent door=Non
- Flush-mounting cabinet Nedbox 12 modules transparent door 201421: Assembly Plastic door 1R=Non; Assembly Plastic door 2R=Non; Assembly Plastic door 3R=Non; Assembly Plastic door 4R=Non; Assembly Plastic door transparent 1R=Oui; Assembly Plastic door transparent 2R=Non; Assembly Plastic door transparent 3R=Non; Assembly Plastic door transparent 4R=Non; Assembly glass metal door 1R=Non; Assembly glass metal door 2R=Non; Assembly glass metal door 3R=Non; Assembly glass metal door 4R=Non; Assembly metal door 1R=Non; Assembly metal door 2R=Non; Assembly metal door 3R=Non; Assembly metal door 4R=Non; Cabinet 001411=Non; Cabinet 001412=Non; Cabinet 001413=Non; Cabinet 001414=Non; Cabinet 001421=Non; Cabinet 001422=Non; Cabinet 001423=Non; Cabinet 001424=Non; Cabinet 001431=Non; Cabinet 001432=Non; Cabinet 001433=Non; Cabinet 001434=Non; Cabinet 001436=Non; Cabinet 001437=Non; Cabinet 001438=Non; Cabinet 001439=Non; Cabinet 001441=Non; Cabinet 001442=Non; Cabinet 001443=Non; Cabinet 001444=Non; Cabinet 001451=Non; Cabinet 001452=Non; Cabinet 001453=Non; Cabinet 001454=Non; Cabinet 201411=Non; Cabinet 201412=Non; Cabinet 201413=Non; Cabinet 201414=Non; Cabinet 201421=Oui; Cabinet 201422=Non; Cabinet 201423=Non; Cabinet 201424=Non; Cabinet 201431=Non; Cabinet 201432=Non; Cabinet 201433=Non; Cabinet 201434=Non; Cabinet HL12F=Non; Cabinet HL24F=Non; Cabinet HL36F=Non; Cabinet HL48F=Non; Number of rows=1; Plastic door=Non; Recessed height=305 mm  [stored 1.00066 ft]; Terminal block E=12 connections Icc 6kA; Terminal block N=12 connections Icc 6kA; glass metal door=Non; height=335 mm  [stored 1.09908 ft]; metal door=Non; transparent door=Oui
- Flush-mounting cabinet Nedbox 24 modules transparent door 201422: Assembly Plastic door 1R=Non; Assembly Plastic door 2R=Non; Assembly Plastic door 3R=Non; Assembly Plastic door 4R=Non; Assembly Plastic door transparent 1R=Non; Assembly Plastic door transparent 2R=Oui; Assembly Plastic door transparent 3R=Non; Assembly Plastic door transparent 4R=Non; Assembly glass metal door 1R=Non; Assembly glass metal door 2R=Non; Assembly glass metal door 3R=Non; Assembly glass metal door 4R=Non; Assembly metal door 1R=Non; Assembly metal door 2R=Non; Assembly metal door 3R=Non; Assembly metal door 4R=Non; Cabinet 001411=Non; Cabinet 001412=Non; Cabinet 001413=Non; Cabinet 001414=Non; Cabinet 001421=Non; Cabinet 001422=Non; Cabinet 001423=Non; Cabinet 001424=Non; Cabinet 001431=Non; Cabinet 001432=Non; Cabinet 001433=Non; Cabinet 001434=Non; Cabinet 001436=Non; Cabinet 001437=Non; Cabinet 001438=Non; Cabinet 001439=Non; Cabinet 001441=Non; Cabinet 001442=Non; Cabinet 001443=Non; Cabinet 001444=Non; Cabinet 001451=Non; Cabinet 001452=Non; Cabinet 001453=Non; Cabinet 001454=Non; Cabinet 201411=Non; Cabinet 201412=Non; Cabinet 201413=Non; Cabinet 201414=Non; Cabinet 201421=Non; Cabinet 201422=Oui; Cabinet 201423=Non; Cabinet 201424=Non; Cabinet 201431=Non; Cabinet 201432=Non; Cabinet 201433=Non; Cabinet 201434=Non; Cabinet HL12F=Non; Cabinet HL24F=Non; Cabinet HL36F=Non; Cabinet HL48F=Non; General Conditions of Use=https://export.legrand.com; Number of rows=2; Plastic door=Non; Recessed height=430 mm; Terminal block E=16 connections Icc 6kA; Terminal block N=2X 8 connections Icc 6kA; glass metal door=Non; height=460 mm  [stored 1.50919 ft]; metal door=Non; transparent door=Oui
- Flush-mounting cabinet Nedbox 36 modules transparent door 201423: Assembly Plastic door 1R=Non; Assembly Plastic door 2R=Non; Assembly Plastic door 3R=Non; Assembly Plastic door 4R=Non; Assembly Plastic door transparent 1R=Non; Assembly Plastic door transparent 2R=Non; Assembly Plastic door transparent 3R=Oui; Assembly Plastic door transparent 4R=Non; Assembly glass metal door 1R=Non; Assembly glass metal door 2R=Non; Assembly glass metal door 3R=Non; Assembly glass metal door 4R=Non; Assembly metal door 1R=Non; Assembly metal door 2R=Non; Assembly metal door 3R=Non; Assembly metal door 4R=Non; Cabinet 001411=Non; Cabinet 001412=Non; Cabinet 001413=Non; Cabinet 001414=Non; Cabinet 001421=Non; Cabinet 001422=Non; Cabinet 001423=Non; Cabinet 001424=Non; Cabinet 001431=Non; Cabinet 001432=Non; Cabinet 001433=Non; Cabinet 001434=Non; Cabinet 001436=Non; Cabinet 001437=Non; Cabinet 001438=Non; Cabinet 001439=Non; Cabinet 001441=Non; Cabinet 001442=Non; Cabinet 001443=Non; Cabinet 001444=Non; Cabinet 001451=Non; Cabinet 001452=Non; Cabinet 001453=Non; Cabinet 001454=Non; Cabinet 201411=Non; Cabinet 201412=Non; Cabinet 201413=Non; Cabinet 201414=Non; Cabinet 201421=Non; Cabinet 201422=Non; Cabinet 201423=Oui; Cabinet 201424=Non; Cabinet 201431=Non; Cabinet 201432=Non; Cabinet 201433=Non; Cabinet 201434=Non; Cabinet HL12F=Non; Cabinet HL24F=Non; Cabinet HL36F=Non; Cabinet HL48F=Non; General Conditions of Use=https://export.legrand.com; Number of rows=3; Plastic door=Non; Recessed height=555 mm  [stored 1.82087 ft]; Terminal block E=30 connections Icc 6kA; Terminal block N=2X 12 connections Icc 6kA; glass metal door=Non; height=585 mm  [stored 1.91929 ft]; metal door=Non; transparent door=Oui
- Flush-mounting cabinet Nedbox 48 modules transparent door 201424: Assembly Plastic door 1R=Non; Assembly Plastic door 2R=Non; Assembly Plastic door 3R=Non; Assembly Plastic door 4R=Non; Assembly Plastic door transparent 1R=Non; Assembly Plastic door transparent 2R=Non; Assembly Plastic door transparent 3R=Non; Assembly Plastic door transparent 4R=Oui; Assembly glass metal door 1R=Non; Assembly glass metal door 2R=Non; Assembly glass metal door 3R=Non; Assembly glass metal door 4R=Non; Assembly metal door 1R=Non; Assembly metal door 2R=Non; Assembly metal door 3R=Non; Assembly metal door 4R=Non; Cabinet 001411=Non; Cabinet 001412=Non; Cabinet 001413=Non; Cabinet 001414=Non; Cabinet 001421=Non; Cabinet 001422=Non; Cabinet 001423=Non; Cabinet 001424=Non; Cabinet 001431=Non; Cabinet 001432=Non; Cabinet 001433=Non; Cabinet 001434=Non; Cabinet 001436=Non; Cabinet 001437=Non; Cabinet 001438=Non; Cabinet 001439=Non; Cabinet 001441=Non; Cabinet 001442=Non; Cabinet 001443=Non; Cabinet 001444=Non; Cabinet 001451=Non; Cabinet 001452=Non; Cabinet 001453=Non; Cabinet 001454=Non; Cabinet 201411=Non; Cabinet 201412=Non; Cabinet 201413=Non; Cabinet 201414=Non; Cabinet 201421=Non; Cabinet 201422=Non; Cabinet 201423=Non; Cabinet 201424=Oui; Cabinet 201431=Non; Cabinet 201432=Non; Cabinet 201433=Non; Cabinet 201434=Non; Cabinet HL12F=Non; Cabinet HL24F=Non; Cabinet HL36F=Non; Cabinet HL48F=Non; General Conditions of Use=https://export.legrand.com; Number of rows=4; Plastic door=Non; Recessed height=680 mm  [stored 2.23097 ft]; Terminal block E=30 connections Icc 6kA; Terminal block N=3X 12 connections Icc 6kA; glass metal door=Non; height=710 mm  [stored 2.3294 ft]; metal door=Non; transparent door=Oui
- Flush-mounting cabinet Nedbox 12 modules metal door 201431: Assembly Plastic door 1R=Non; Assembly Plastic door 2R=Non; Assembly Plastic door 3R=Non; Assembly Plastic door 4R=Non; Assembly Plastic door transparent 1R=Non; Assembly Plastic door transparent 2R=Non; Assembly Plastic door transparent 3R=Non; Assembly Plastic door transparent 4R=Non; Assembly glass metal door 1R=Non; Assembly glass metal door 2R=Non; Assembly glass metal door 3R=Non; Assembly glass metal door 4R=Non; Assembly metal door 1R=Oui; Assembly metal door 2R=Non; Assembly metal door 3R=Non; Assembly metal door 4R=Non; Cabinet 001411=Non; Cabinet 001412=Non; Cabinet 001413=Non; Cabinet 001414=Non; Cabinet 001421=Non; Cabinet 001422=Non; Cabinet 001423=Non; Cabinet 001424=Non; Cabinet 001431=Non; Cabinet 001432=Non; Cabinet 001433=Non; Cabinet 001434=Non; Cabinet 001436=Non; Cabinet 001437=Non; Cabinet 001438=Non; Cabinet 001439=Non; Cabinet 001441=Non; Cabinet 001442=Non; Cabinet 001443=Non; Cabinet 001444=Non; Cabinet 001451=Non; Cabinet 001452=Non; Cabinet 001453=Non; Cabinet 001454=Non; Cabinet 201411=Non; Cabinet 201412=Non; Cabinet 201413=Non; Cabinet 201414=Non; Cabinet 201421=Non; Cabinet 201422=Non; Cabinet 201423=Non; Cabinet 201424=Non; Cabinet 201431=Oui; Cabinet 201432=Non; Cabinet 201433=Non; Cabinet 201434=Non; Cabinet HL12F=Non; Cabinet HL24F=Non; Cabinet HL36F=Non; Cabinet HL48F=Non; Number of rows=1; Plastic door=Non; Recessed height=305 mm  [stored 1.00066 ft]; Terminal block E=12 connections Icc 6kA; Terminal block N=12 connections Icc 6kA; glass metal door=Non; height=335 mm  [stored 1.09908 ft]; metal door=Oui; transparent door=Non
- Flush-mounting cabinet Nedbox 24 modules metal door 201432: Assembly Plastic door 1R=Non; Assembly Plastic door 2R=Non; Assembly Plastic door 3R=Non; Assembly Plastic door 4R=Non; Assembly Plastic door transparent 1R=Non; Assembly Plastic door transparent 2R=Non; Assembly Plastic door transparent 3R=Non; Assembly Plastic door transparent 4R=Non; Assembly glass metal door 1R=Non; Assembly glass metal door 2R=Non; Assembly glass metal door 3R=Non; Assembly glass metal door 4R=Non; Assembly metal door 1R=Non; Assembly metal door 2R=Oui; Assembly metal door 3R=Non; Assembly metal door 4R=Non; Cabinet 001411=Non; Cabinet 001412=Non; Cabinet 001413=Non; Cabinet 001414=Non; Cabinet 001421=Non; Cabinet 001422=Non; Cabinet 001423=Non; Cabinet 001424=Non; Cabinet 001431=Non; Cabinet 001432=Non; Cabinet 001433=Non; Cabinet 001434=Non; Cabinet 001436=Non; Cabinet 001437=Non; Cabinet 001438=Non; Cabinet 001439=Non; Cabinet 001441=Non; Cabinet 001442=Non; Cabinet 001443=Non; Cabinet 001444=Non; Cabinet 001451=Non; Cabinet 001452=Non; Cabinet 001453=Non; Cabinet 001454=Non; Cabinet 201411=Non; Cabinet 201412=Non; Cabinet 201413=Non; Cabinet 201414=Non; Cabinet 201421=Non; Cabinet 201422=Non; Cabinet 201423=Non; Cabinet 201424=Non; Cabinet 201431=Non; Cabinet 201432=Oui; Cabinet 201433=Non; Cabinet 201434=Non; Cabinet HL12F=Non; Cabinet HL24F=Non; Cabinet HL36F=Non; Cabinet HL48F=Non; General Conditions of Use=https://export.legrand.com; Number of rows=2; Plastic door=Non; Recessed height=430 mm; Terminal block E=16 connections Icc 6kA; Terminal block N=2X 8 connections Icc 6kA; glass metal door=Non; height=460 mm  [stored 1.50919 ft]; metal door=Oui; transparent door=Non
- Flush-mounting cabinet Nedbox 36 modules metal door 201433: Assembly Plastic door 1R=Non; Assembly Plastic door 2R=Non; Assembly Plastic door 3R=Non; Assembly Plastic door 4R=Non; Assembly Plastic door transparent 1R=Non; Assembly Plastic door transparent 2R=Non; Assembly Plastic door transparent 3R=Non; Assembly Plastic door transparent 4R=Non; Assembly glass metal door 1R=Non; Assembly glass metal door 2R=Non; Assembly glass metal door 3R=Non; Assembly glass metal door 4R=Non; Assembly metal door 1R=Non; Assembly metal door 2R=Non; Assembly metal door 3R=Oui; Assembly metal door 4R=Non; Cabinet 001411=Non; Cabinet 001412=Non; Cabinet 001413=Non; Cabinet 001414=Non; Cabinet 001421=Non; Cabinet 001422=Non; Cabinet 001423=Non; Cabinet 001424=Non; Cabinet 001431=Non; Cabinet 001432=Non; Cabinet 001433=Non; Cabinet 001434=Non; Cabinet 001436=Non; Cabinet 001437=Non; Cabinet 001438=Non; Cabinet 001439=Non; Cabinet 001441=Non; Cabinet 001442=Non; Cabinet 001443=Non; Cabinet 001444=Non; Cabinet 001451=Non; Cabinet 001452=Non; Cabinet 001453=Non; Cabinet 001454=Non; Cabinet 201411=Non; Cabinet 201412=Non; Cabinet 201413=Non; Cabinet 201414=Non; Cabinet 201421=Non; Cabinet 201422=Non; Cabinet 201423=Non; Cabinet 201424=Non; Cabinet 201431=Non; Cabinet 201432=Non; Cabinet 201433=Oui; Cabinet 201434=Non; Cabinet HL12F=Non; Cabinet HL24F=Non; Cabinet HL36F=Non; Cabinet HL48F=Non; General Conditions of Use=https://export.legrand.com; Number of rows=3; Plastic door=Non; Recessed height=555 mm  [stored 1.82087 ft]; Terminal block E=30 connections Icc 6kA; Terminal block N=2X 12 connections Icc 6kA; glass metal door=Non; height=585 mm  [stored 1.91929 ft]; metal door=Oui; transparent door=Non
- Flush-mounting cabinet Nedbox 48 modules metal door 201434: Assembly Plastic door 1R=Non; Assembly Plastic door 2R=Non; Assembly Plastic door 3R=Non; Assembly Plastic door 4R=Non; Assembly Plastic door transparent 1R=Non; Assembly Plastic door transparent 2R=Non; Assembly Plastic door transparent 3R=Non; Assembly Plastic door transparent 4R=Non; Assembly glass metal door 1R=Non; Assembly glass metal door 2R=Non; Assembly glass metal door 3R=Non; Assembly glass metal door 4R=Non; Assembly metal door 1R=Non; Assembly metal door 2R=Non; Assembly metal door 3R=Non; Assembly metal door 4R=Oui; Cabinet 001411=Non; Cabinet 001412=Non; Cabinet 001413=Non; Cabinet 001414=Non; Cabinet 001421=Non; Cabinet 001422=Non; Cabinet 001423=Non; Cabinet 001424=Non; Cabinet 001431=Non; Cabinet 001432=Non; Cabinet 001433=Non; Cabinet 001434=Non; Cabinet 001436=Non; Cabinet 001437=Non; Cabinet 001438=Non; Cabinet 001439=Non; Cabinet 001441=Non; Cabinet 001442=Non; Cabinet 001443=Non; Cabinet 001444=Non; Cabinet 001451=Non; Cabinet 001452=Non; Cabinet 001453=Non; Cabinet 001454=Non; Cabinet 201411=Non; Cabinet 201412=Non; Cabinet 201413=Non; Cabinet 201414=Non; Cabinet 201421=Non; Cabinet 201422=Non; Cabinet 201423=Non; Cabinet 201424=Non; Cabinet 201431=Non; Cabinet 201432=Non; Cabinet 201433=Non; Cabinet 201434=Oui; Cabinet HL12F=Non; Cabinet HL24F=Non; Cabinet HL36F=Non; Cabinet HL48F=Non; General Conditions of Use=https://export.legrand.com; Number of rows=4; Plastic door=Non; Recessed height=680 mm  [stored 2.23097 ft]; Terminal block E=30 connections Icc 6kA; Terminal block N=3X 12 connections Icc 6kA; glass metal door=Non; height=710 mm  [stored 2.3294 ft]; metal door=Oui; transparent door=Non
- Flush-mounting cabinet Nedbox 12 modules Plastic door HL12F: Assembly Plastic door 1R=Oui; Assembly Plastic door 2R=Non; Assembly Plastic door 3R=Non; Assembly Plastic door 4R=Non; Assembly Plastic door transparent 1R=Non; Assembly Plastic door transparent 2R=Non; Assembly Plastic door transparent 3R=Non; Assembly Plastic door transparent 4R=Non; Assembly glass metal door 1R=Non; Assembly glass metal door 2R=Non; Assembly glass metal door 3R=Non; Assembly glass metal door 4R=Non; Assembly metal door 1R=Non; Assembly metal door 2R=Non; Assembly metal door 3R=Non; Assembly metal door 4R=Non; Cabinet 001411=Non; Cabinet 001412=Non; Cabinet 001413=Non; Cabinet 001414=Non; Cabinet 001421=Non; Cabinet 001422=Non; Cabinet 001423=Non; Cabinet 001424=Non; Cabinet 001431=Non; Cabinet 001432=Non; Cabinet 001433=Non; Cabinet 001434=Non; Cabinet 001436=Non; Cabinet 001437=Non; Cabinet 001438=Non; Cabinet 001439=Non; Cabinet 001441=Non; Cabinet 001442=Non; Cabinet 001443=Non; Cabinet 001444=Non; Cabinet 001451=Non; Cabinet 001452=Non; Cabinet 001453=Non; Cabinet 001454=Non; Cabinet 201411=Non; Cabinet 201412=Non; Cabinet 201413=Non; Cabinet 201414=Non; Cabinet 201421=Non; Cabinet 201422=Non; Cabinet 201423=Non; Cabinet 201424=Non; Cabinet 201431=Non; Cabinet 201432=Non; Cabinet 201433=Non; Cabinet 201434=Non; Cabinet HL12F=Oui; Cabinet HL24F=Non; Cabinet HL36F=Non; Cabinet HL48F=Non; Number of rows=1; Plastic door=Oui; Recessed height=305 mm  [stored 1.00066 ft]; Terminal block E=8 connections Icc 10kA; Terminal block N=13 connections Icc 10kA +2X 4 connections Icc 10kA; glass metal door=Non; height=335 mm  [stored 1.09908 ft]; metal door=Non; transparent door=Non
- Flush-mounting cabinet Nedbox 24 modules Plastic door HL24F: Assembly Plastic door 1R=Non; Assembly Plastic door 2R=Oui; Assembly Plastic door 3R=Non; Assembly Plastic door 4R=Non; Assembly Plastic door transparent 1R=Non; Assembly Plastic door transparent 2R=Non; Assembly Plastic door transparent 3R=Non; Assembly Plastic door transparent 4R=Non; Assembly glass metal door 1R=Non; Assembly glass metal door 2R=Non; Assembly glass metal door 3R=Non; Assembly glass metal door 4R=Non; Assembly metal door 1R=Non; Assembly metal door 2R=Non; Assembly metal door 3R=Non; Assembly metal door 4R=Non; Cabinet 001411=Non; Cabinet 001412=Non; Cabinet 001413=Non; Cabinet 001414=Non; Cabinet 001421=Non; Cabinet 001422=Non; Cabinet 001423=Non; Cabinet 001424=Non; Cabinet 001431=Non; Cabinet 001432=Non; Cabinet 001433=Non; Cabinet 001434=Non; Cabinet 001436=Non; Cabinet 001437=Non; Cabinet 001438=Non; Cabinet 001439=Non; Cabinet 001441=Non; Cabinet 001442=Non; Cabinet 001443=Non; Cabinet 001444=Non; Cabinet 001451=Non; Cabinet 001452=Non; Cabinet 001453=Non; Cabinet 001454=Non; Cabinet 201411=Non; Cabinet 201412=Non; Cabinet 201413=Non; Cabinet 201414=Non; Cabinet 201421=Non; Cabinet 201422=Non; Cabinet 201423=Non; Cabinet 201424=Non; Cabinet 201431=Non; Cabinet 201432=Non; Cabinet 201433=Non; Cabinet 201434=Non; Cabinet HL12F=Non; Cabinet HL24F=Oui; Cabinet HL36F=Non; Cabinet HL48F=Non; General Conditions of Use=https://export.legrand.com; Number of rows=2; Plastic door=Oui; Recessed height=430 mm; Terminal block E=17 connections Icc 10kA; Terminal block N=13 connections Icc 10kA +2X 8 connections Icc 10kA; glass metal door=Non; height=460 mm  [stored 1.50919 ft]; metal door=Non; transparent door=Non
- Flush-mounting cabinet Nedbox 36 modules Plastic door HL36F: Assembly Plastic door 1R=Non; Assembly Plastic door 2R=Non; Assembly Plastic door 3R=Oui; Assembly Plastic door 4R=Non; Assembly Plastic door transparent 1R=Non; Assembly Plastic door transparent 2R=Non; Assembly Plastic door transparent 3R=Non; Assembly Plastic door transparent 4R=Non; Assembly glass metal door 1R=Non; Assembly glass metal door 2R=Non; Assembly glass metal door 3R=Non; Assembly glass metal door 4R=Non; Assembly metal door 1R=Non; Assembly metal door 2R=Non; Assembly metal door 3R=Non; Assembly metal door 4R=Non; Cabinet 001411=Non; Cabinet 001412=Non; Cabinet 001413=Non; Cabinet 001414=Non; Cabinet 001421=Non; Cabinet 001422=Non; Cabinet 001423=Non; Cabinet 001424=Non; Cabinet 001431=Non; Cabinet 001432=Non; Cabinet 001433=Non; Cabinet 001434=Non; Cabinet 001436=Non; Cabinet 001437=Non; Cabinet 001438=Non; Cabinet 001439=Non; Cabinet 001441=Non; Cabinet 001442=Non; Cabinet 001443=Non; Cabinet 001444=Non; Cabinet 001451=Non; Cabinet 001452=Non; Cabinet 001453=Non; Cabinet 001454=Non; Cabinet 201411=Non; Cabinet 201412=Non; Cabinet 201413=Non; Cabinet 201414=Non; Cabinet 201421=Non; Cabinet 201422=Non; Cabinet 201423=Non; Cabinet 201424=Non; Cabinet 201431=Non; Cabinet 201432=Non; Cabinet 201433=Non; Cabinet 201434=Non; Cabinet HL12F=Non; Cabinet HL24F=Non; Cabinet HL36F=Oui; Cabinet HL48F=Non; General Conditions of Use=https://export.legrand.com; Number of rows=3; Plastic door=Oui; Recessed height=555 mm  [stored 1.82087 ft]; Terminal block E=22 connections Icc 10kA; Terminal block N=13 connections Icc 10kA +2X 8 connections Icc 10kA; glass metal door=Non; height=585 mm  [stored 1.91929 ft]; metal door=Non; transparent door=Non
- Flush-mounting cabinet Nedbox 48 modules Plastic door HL48F: Assembly Plastic door 1R=Non; Assembly Plastic door 2R=Non; Assembly Plastic door 3R=Non; Assembly Plastic door 4R=Oui; Assembly Plastic door transparent 1R=Non; Assembly Plastic door transparent 2R=Non; Assembly Plastic door transparent 3R=Non; Assembly Plastic door transparent 4R=Non; Assembly glass metal door 1R=Non; Assembly glass metal door 2R=Non; Assembly glass metal door 3R=Non; Assembly glass metal door 4R=Non; Assembly metal door 1R=Non; Assembly metal door 2R=Non; Assembly metal door 3R=Non; Assembly metal door 4R=Non; Cabinet 001411=Non; Cabinet 001412=Non; Cabinet 001413=Non; Cabinet 001414=Non; Cabinet 001421=Non; Cabinet 001422=Non; Cabinet 001423=Non; Cabinet 001424=Non; Cabinet 001431=Non; Cabinet 001432=Non; Cabinet 001433=Non; Cabinet 001434=Non; Cabinet 001436=Non; Cabinet 001437=Non; Cabinet 001438=Non; Cabinet 001439=Non; Cabinet 001441=Non; Cabinet 001442=Non; Cabinet 001443=Non; Cabinet 001444=Non; Cabinet 001451=Non; Cabinet 001452=Non; Cabinet 001453=Non; Cabinet 001454=Non; Cabinet 201411=Non; Cabinet 201412=Non; Cabinet 201413=Non; Cabinet 201414=Non; Cabinet 201421=Non; Cabinet 201422=Non; Cabinet 201423=Non; Cabinet 201424=Non; Cabinet 201431=Non; Cabinet 201432=Non; Cabinet 201433=Non; Cabinet 201434=Non; Cabinet HL12F=Non; Cabinet HL24F=Non; Cabinet HL36F=Non; Cabinet HL48F=Oui; General Conditions of Use=https://export.legrand.com; Number of rows=4; Plastic door=Oui; Recessed height=680 mm  [stored 2.23097 ft]; Terminal block E=27 connections Icc 10kA; Terminal block N=2X 13 connections Icc 10kA +2X 8 connections Icc 10kA; glass metal door=Non; height=710 mm  [stored 2.3294 ft]; metal door=Non; transparent door=Non

note: [stored X ft] marks values corroborated as IEEE doubles in the binary element streams (Revit-internal decimal feet)
